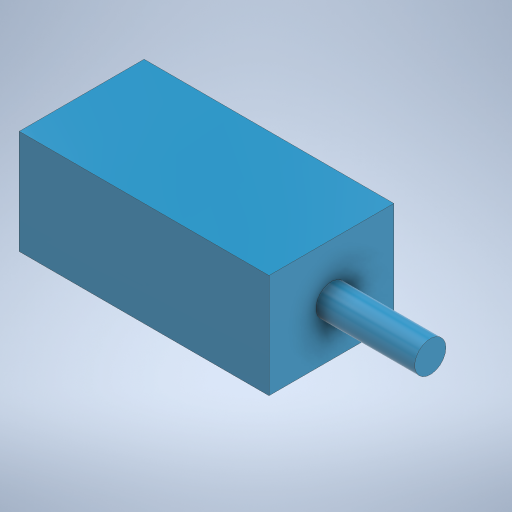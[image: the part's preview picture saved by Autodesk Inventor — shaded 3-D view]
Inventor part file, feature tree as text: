
AUTODESK INVENTOR PART (.ipt)
format: ipt  version: 2024 (Build 280153020, 153B)  size: 232,448 bytes
history: native  units: mm
features: extrude x2, sketch x2
ambient origin geometry x8: Origin, YZ Plane, XZ Plane, XY Plane, X Axis, Y Axis, Z Axis, Center Point
bodies: Solid1 (feature_tree)
feature tree (4):
  extrude  "Extrusion1"  Depth=12.0mm
  extrude  "Extrusion2"  Depth=9.5mm
  sketch  "Sketch1"  dims[d0=24.0mm d1=12.0mm]
  sketch  "Sketch2"  dims[d2=10.0mm d3=0.0mm d4=3.0mm d5=9.5mm d6=0.0mm]
